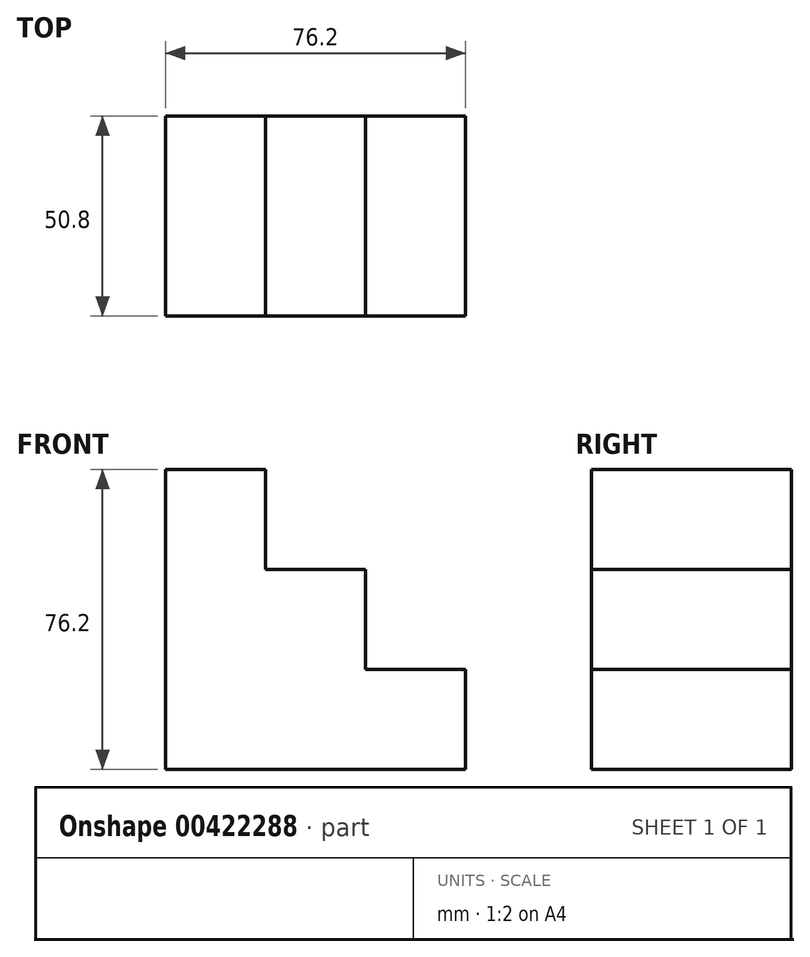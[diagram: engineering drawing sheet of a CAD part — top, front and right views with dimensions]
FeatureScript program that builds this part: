
annotation { "Feature Type Name" : "Feature", "Feature Type Description" : "" }
export const myFeature = defineFeature(function(context is Context, id is Id, definition is map)
    precondition{}
    {
        {
            var Q0;
            Q0=qCreatedBy(makeId("Front.planeOp"),FACE);
            var sketch = newSketch(context, id + "F0", { "sketchPlane" : qUnion([Q0])});
            skLineSegment(sketch, "E0", {"start": v(-63.52, 67.2) * mm, "end": v(-63.52, -9) * mm});
            skLineSegment(sketch, "E1", {"start": v(-63.52, -9) * mm, "end": v(12.68, -9) * mm});
            skLineSegment(sketch, "E2", {"start": v(12.68, -9) * mm, "end": v(12.68, 16.4) * mm});
            skLineSegment(sketch, "E3", {"start": v(12.68, 16.4) * mm, "end": v(-12.72, 16.4) * mm});
            skLineSegment(sketch, "E4", {"start": v(-12.72, 16.4) * mm, "end": v(-12.72, 41.8) * mm});
            skLineSegment(sketch, "E5", {"start": v(-12.72, 41.8) * mm, "end": v(-38.12, 41.8) * mm});
            skLineSegment(sketch, "E6", {"start": v(-38.12, 41.8) * mm, "end": v(-38.12, 67.2) * mm});
            skLineSegment(sketch, "E7", {"start": v(-38.12, 67.2) * mm, "end": v(-63.52, 67.2) * mm});
            skSolve(sketch);
        }
        {
            var Q0;
            Q0 = qSketchRegion(id + "F0", true);
            extrude(context, id + "F1", {"entities" : qUnion([Q0]), "depth" : 50.8 * mm});
        }
    });
